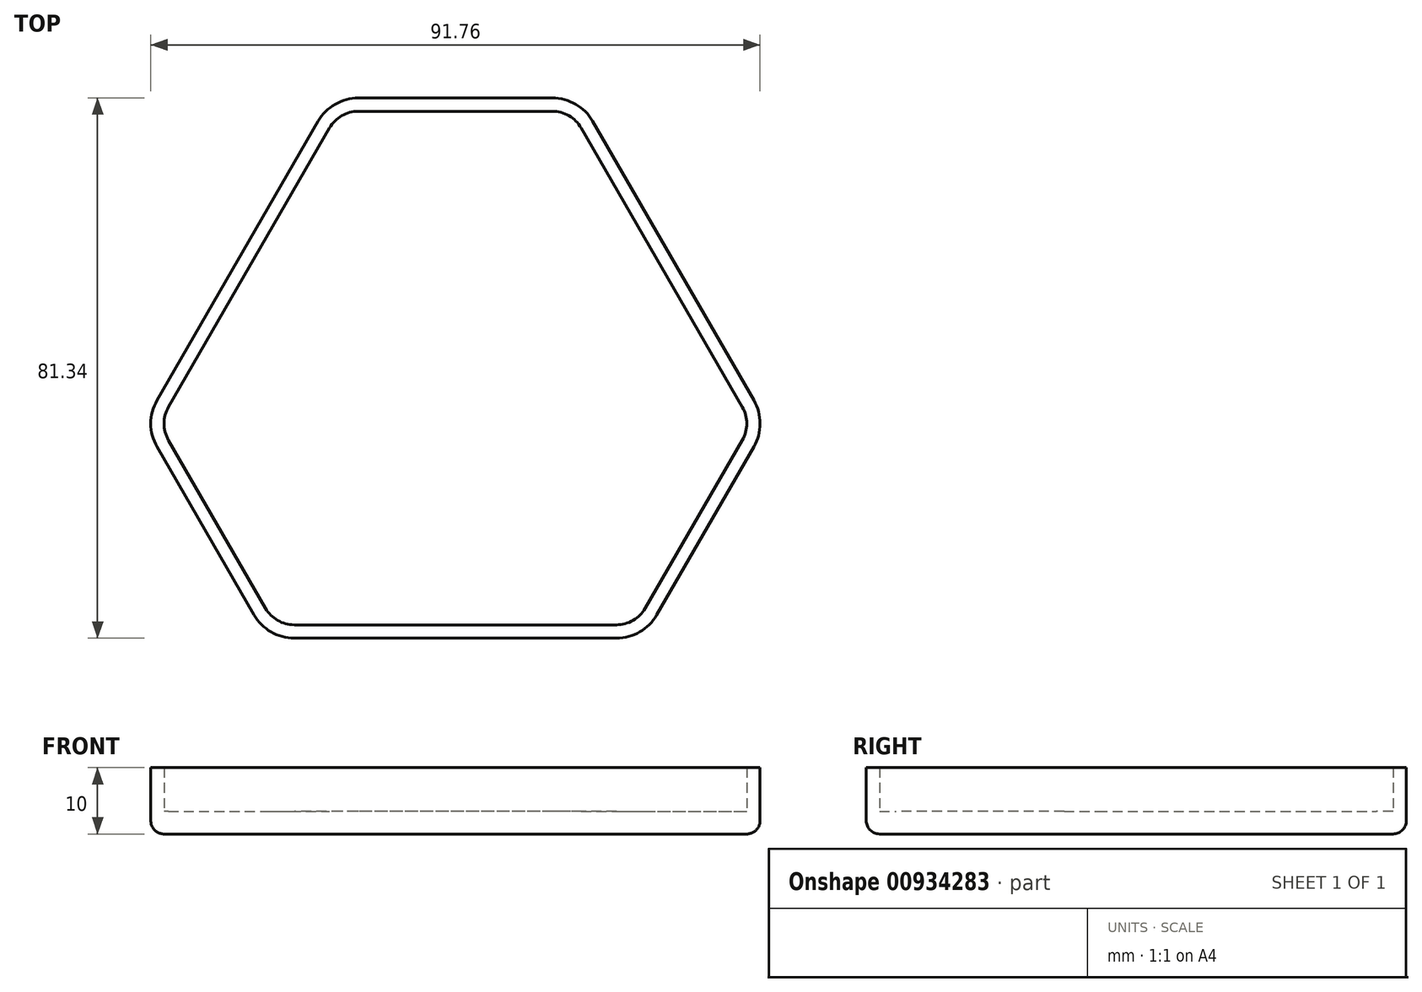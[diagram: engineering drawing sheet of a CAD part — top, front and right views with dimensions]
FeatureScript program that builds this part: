
annotation { "Feature Type Name" : "Feature", "Feature Type Description" : "" }
export const myFeature = defineFeature(function(context is Context, id is Id, definition is map)
    precondition{}
    {
        {
            var Q0;
            Q0=qCreatedBy(makeId("Top.planeOp"),FACE);
            var sketch = newSketch(context, id + "F0", { "sketchPlane" : qUnion([Q0])});
            skCircle(sketch, "E0", {"center": v(0, 0) * mm, "radius": 45 * mm, "construction": true});
            skLineSegment(sketch, "E1", {"start": v(14.61, 41.46) * mm, "end": v(-14.61, 41.46) * mm});
            skLineSegment(sketch, "E2.1.0", {"start": v(-43.21, -8.07) * mm, "end": v(-28.6, -33.38) * mm});
            skLineSegment(sketch, "E2.2.0", {"start": v(28.6, -33.38) * mm, "end": v(43.21, -8.07) * mm});
            skLineSegment(sketch, "E3", {"start": v(-43.21, -3.07) * mm, "end": v(-18.94, 38.96) * mm});
            skLineSegment(sketch, "E4", {"start": v(18.94, 38.96) * mm, "end": v(43.21, -3.07) * mm});
            skLineSegment(sketch, "E5", {"start": v(24.27, -35.88) * mm, "end": v(-24.27, -35.88) * mm});
            skPoint(sketch, "E6.visualSharp", {"position": v(-17.5, 41.46) * mm});
            skArc(sketch, "E6.filletArc", {"start": v(-14.61, 41.46) * mm, "mid": v(-17.11, 40.79) * mm, "end": v(-18.94, 38.96) * mm});
            skPoint(sketch, "E7.visualSharp", {"position": v(17.5, 41.46) * mm});
            skArc(sketch, "E7.filletArc", {"start": v(18.94, 38.96) * mm, "mid": v(17.11, 40.79) * mm, "end": v(14.61, 41.46) * mm});
            skPoint(sketch, "E8.visualSharp", {"position": v(44.65, -5.57) * mm});
            skArc(sketch, "E8.filletArc", {"start": v(43.21, -8.07) * mm, "mid": v(43.88, -5.57) * mm, "end": v(43.21, -3.07) * mm});
            skPoint(sketch, "E9.visualSharp", {"position": v(-44.65, -5.57) * mm});
            skArc(sketch, "E9.filletArc", {"start": v(-43.21, -3.07) * mm, "mid": v(-43.88, -5.57) * mm, "end": v(-43.21, -8.07) * mm});
            skPoint(sketch, "E10.visualSharp", {"position": v(-27.15, -35.88) * mm});
            skArc(sketch, "E10.filletArc", {"start": v(-28.6, -33.38) * mm, "mid": v(-26.77, -35.21) * mm, "end": v(-24.27, -35.88) * mm});
            skPoint(sketch, "E11.visualSharp", {"position": v(27.15, -35.88) * mm});
            skArc(sketch, "E11.filletArc", {"start": v(24.27, -35.88) * mm, "mid": v(26.77, -35.21) * mm, "end": v(28.6, -33.38) * mm});
            skArc(sketch, "E12.0", {"start": v(20.68, 39.96) * mm, "mid": v(18.11, 42.52) * mm, "end": v(14.61, 43.46) * mm});
            skLineSegment(sketch, "E12.1", {"start": v(-44.94, -9.07) * mm, "end": v(-30.33, -34.38) * mm});
            skArc(sketch, "E12.2", {"start": v(-44.94, -2.07) * mm, "mid": v(-45.88, -5.57) * mm, "end": v(-44.94, -9.07) * mm});
            skLineSegment(sketch, "E12.3", {"start": v(-44.94, -2.07) * mm, "end": v(-20.68, 39.96) * mm});
            skArc(sketch, "E12.4", {"start": v(-14.61, 43.46) * mm, "mid": v(-18.11, 42.52) * mm, "end": v(-20.68, 39.96) * mm});
            skArc(sketch, "E12.5", {"start": v(-30.33, -34.38) * mm, "mid": v(-27.77, -36.95) * mm, "end": v(-24.27, -37.88) * mm});
            skLineSegment(sketch, "E12.6", {"start": v(14.61, 43.46) * mm, "end": v(-14.61, 43.46) * mm});
            skLineSegment(sketch, "E12.7", {"start": v(24.27, -37.88) * mm, "end": v(-24.27, -37.88) * mm});
            skArc(sketch, "E12.8", {"start": v(24.27, -37.88) * mm, "mid": v(27.77, -36.95) * mm, "end": v(30.33, -34.38) * mm});
            skLineSegment(sketch, "E12.9", {"start": v(30.33, -34.38) * mm, "end": v(44.94, -9.07) * mm});
            skArc(sketch, "E12.10", {"start": v(44.94, -9.07) * mm, "mid": v(45.88, -5.57) * mm, "end": v(44.94, -2.07) * mm});
            skLineSegment(sketch, "E12.11", {"start": v(20.68, 39.96) * mm, "end": v(44.94, -2.07) * mm});
            skSolve(sketch);
        }
        {
            var Q0;
            Q0=makeQuery(id+"F0.imprint","IMPRINT",FACE,{"disambiguationData":[TD([[makeQuery(id+"F0.imprint","IMPRINT",EDGE,{"derivedFrom":sQuery(id+"F0.wireOp",EDGE,"E1")}),1.0]])]});
            extrude(context, id + "F1", {"entities" : qUnion([Q0]), "depth" : 3.4 * mm, "offsetDistance" : 25 * mm});
        }
        {
            var Q0;
            Q0=makeQuery(id+"F0.imprint","IMPRINT",FACE,{"disambiguationData":[TD([[makeQuery(id+"F0.imprint","IMPRINT",EDGE,{"derivedFrom":sQuery(id+"F0.wireOp",EDGE,"E1")}),-1.0]])]});
            extrude(context, id + "F2", {"entities" : qUnion([Q0]), "operationType" : NewBodyOperationType.ADD, "depth" : 10 * mm, "offsetDistance" : 25 * mm});
        }
        {
            var Q0;
            Q0=makeQuery(id+"F2.opExtrude","CAP_EDGE",EDGE,{"disambiguationData":[OSD([sQuery(id+"F0.wireOp",EDGE,"E12.11")])],"isStart":true});
            fillet(context, id + "F3", {"entities" : qUnion([Q0]), "radius" : 2 * mm, "tangentPropagation" : true, "allowEdgeOverflow" : false});
        }
    });
